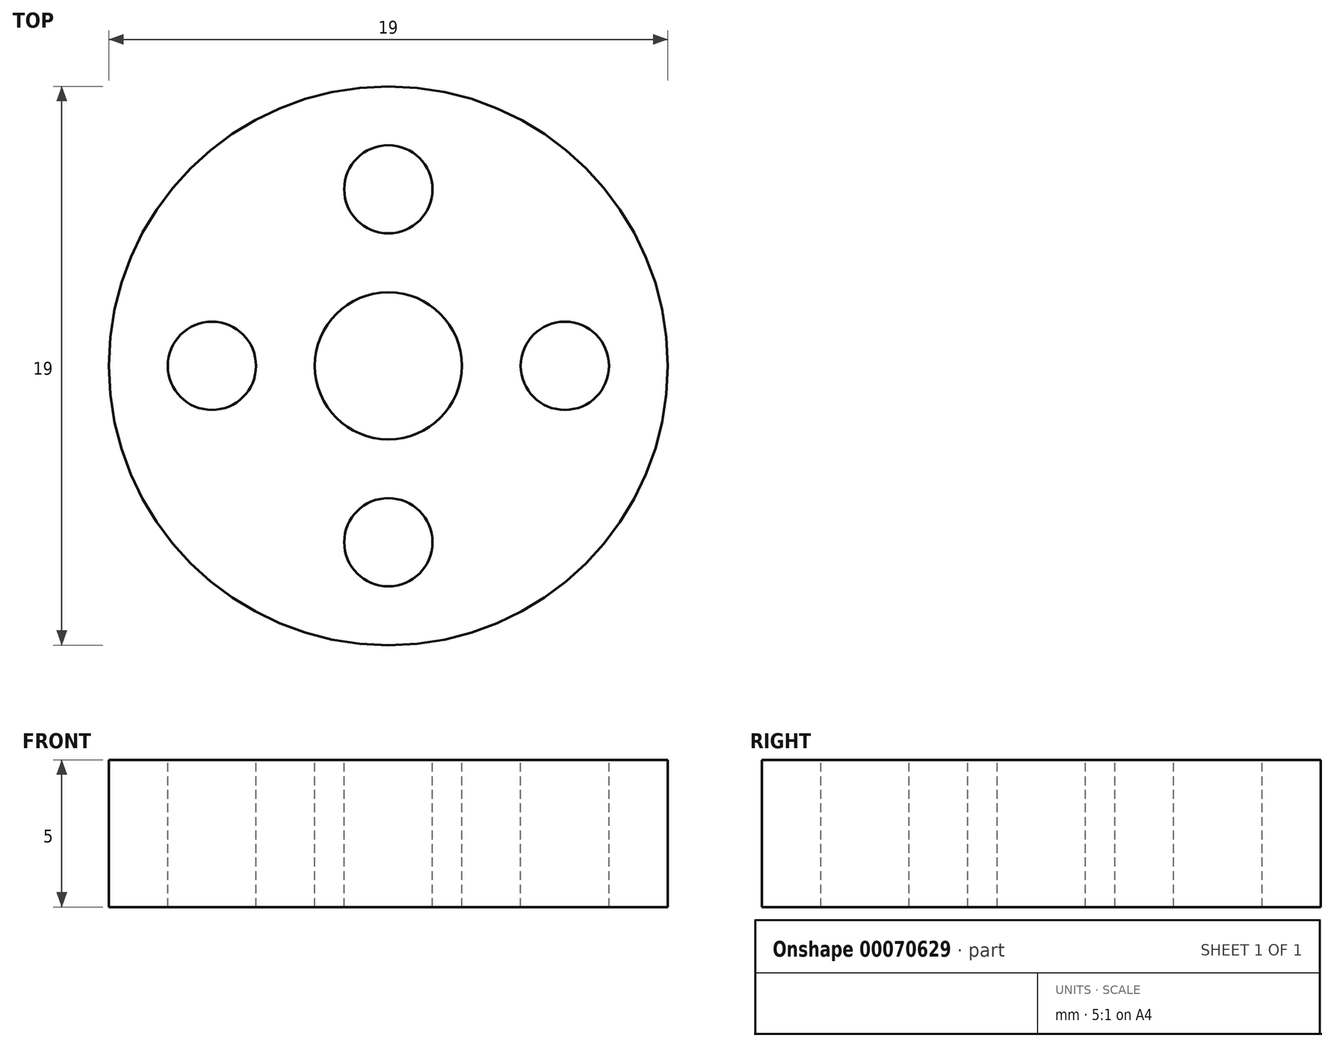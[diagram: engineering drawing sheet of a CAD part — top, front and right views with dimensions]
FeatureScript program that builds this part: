
annotation { "Feature Type Name" : "Feature", "Feature Type Description" : "" }
export const myFeature = defineFeature(function(context is Context, id is Id, definition is map)
    precondition{}
    {
        {
            var Q0;
            Q0=qCreatedBy(makeId("Top.planeOp"),FACE);
            var sketch = newSketch(context, id + "F0", { "sketchPlane" : qUnion([Q0])});
            skCircle(sketch, "E0", {"center": v(0, 0) * mm, "radius": 9.5 * mm});
            skCircle(sketch, "E1", {"center": v(0, 0) * mm, "radius": 2.5 * mm});
            skCircle(sketch, "E2.1.0", {"center": v(-6, 0) * mm, "radius": 1.5 * mm});
            skLineSegment(sketch, "E3", {"start": v(-2.5, 0) * mm, "end": v(-9.5, 0) * mm});
            skCircle(sketch, "E4.1.0", {"center": v(0, -6) * mm, "radius": 1.5 * mm});
            skCircle(sketch, "E4.2.0", {"center": v(6, 0) * mm, "radius": 1.5 * mm});
            skCircle(sketch, "E4.3.0", {"center": v(0, 6) * mm, "radius": 1.5 * mm});
            skSolve(sketch);
        }
        {
            var Q0;
            Q0=makeQuery(id+"F0.imprint","IMPRINT",FACE,{"disambiguationData":[TD([[makeQuery(id+"F0.imprint","IMPRINT",EDGE,{"derivedFrom":sQuery(id+"F0.wireOp",EDGE,"E0")}),1.0]])]});
            extrude(context, id + "F1", {"entities" : qUnion([Q0]), "oppositeDirection" : true, "depth" : 5 * mm});
        }
    });
